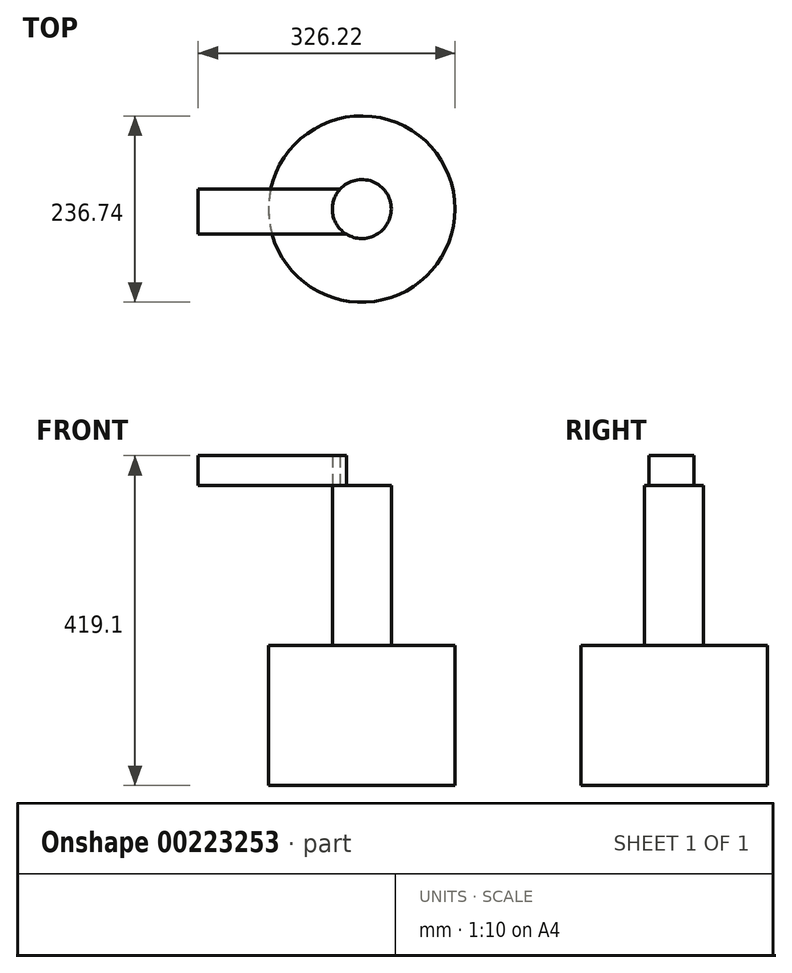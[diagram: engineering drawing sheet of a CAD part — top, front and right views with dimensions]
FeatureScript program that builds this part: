
annotation { "Feature Type Name" : "Feature", "Feature Type Description" : "" }
export const myFeature = defineFeature(function(context is Context, id is Id, definition is map)
    precondition{}
    {
        {
            var Q0;
            Q0=qCreatedBy(makeId("Top.planeOp"),FACE);
            var sketch = newSketch(context, id + "F0", { "sketchPlane" : qUnion([Q0])});
            skCircle(sketch, "E0", {"center": v(0, 0) * mm, "radius": 118.37 * mm});
            skSolve(sketch);
        }
        {
            var Q0;
            Q0=makeQuery(id+"F0.imprint","IMPRINT",FACE,{"disambiguationData":[TD([[makeQuery(id+"F0.imprint","IMPRINT",EDGE,{"derivedFrom":sQuery(id+"F0.wireOp",EDGE,"E0")}),1.0]])]});
            extrude(context, id + "F1", {"entities" : qUnion([Q0]), "depth" : 177.8 * mm});
        }
        {
            var Q0;
            Q0=makeQuery(id+"F1.opExtrude","CAP_FACE",FACE,{"disambiguationData":[OSD([sQuery(id+"F0.wireOp",EDGE,"E0")])],"isStart":false});
            var sketch = newSketch(context, id + "F2", { "sketchPlane" : qUnion([Q0])});
            skCircle(sketch, "E1", {"center": v(0, 0) * mm, "radius": 37.45 * mm});
            skSolve(sketch);
        }
        {
            var Q0;
            Q0=makeQuery(id+"F2.imprint","IMPRINT",FACE,{"disambiguationData":[TD([[makeQuery(id+"F2.imprint","IMPRINT",EDGE,{"derivedFrom":sQuery(id+"F2.wireOp",EDGE,"E1")}),1.0]])]});
            extrude(context, id + "F3", {"entities" : qUnion([Q0]), "operationType" : NewBodyOperationType.ADD, "depth" : 203.2 * mm});
        }
        {
            var Q0;
            Q0=makeQuery(id+"F3.opExtrude","CAP_FACE",FACE,{"disambiguationData":[OSD([sQuery(id+"F2.wireOp",EDGE,"E1")])],"isStart":false});
            var sketch = newSketch(context, id + "F4", { "sketchPlane" : qUnion([Q0])});
            skLineSegment(sketch, "E2.top", {"start": v(0, 25.23) * mm, "end": v(83.63, 25.23) * mm});
            skLineSegment(sketch, "E2.right", {"start": v(83.63, 0) * mm, "end": v(83.63, 25.23) * mm});
            skLineSegment(sketch, "E3.top", {"start": v(0, -32.01) * mm, "end": v(-207.85, -32.01) * mm});
            skLineSegment(sketch, "E3.right", {"start": v(-207.85, 0) * mm, "end": v(-207.85, -32.01) * mm});
            skLineSegment(sketch, "E4.bottom", {"start": v(83.63, 25.23) * mm, "end": v(-207.85, 25.23) * mm});
            skLineSegment(sketch, "E4.top", {"start": v(83.63, -32.01) * mm, "end": v(-207.85, -32.01) * mm});
            skLineSegment(sketch, "E4.left", {"start": v(83.63, 25.23) * mm, "end": v(83.63, -32.01) * mm});
            skLineSegment(sketch, "E4.right", {"start": v(-207.85, 25.23) * mm, "end": v(-207.85, -32.01) * mm});
            skSolve(sketch);
        }
        {
            var Q0;
            {var subQ0=sQuery(id+"F4.wireOp",EDGE,"E4.right");var subQ1=sQuery(id+"F4.wireOp",EDGE,"E4.bottom");var subQ2=makeQuery(id+"F4.imprint","INTERSECT",VERTEX,{"derivedFrom":[subQ1,subQ0]});Q0=makeQuery(id+"F4.imprint","IMPRINT",FACE,{"disambiguationData":[TD([[makeQuery(id+"F4.imprint","IMPRINT",EDGE,{"disambiguationData":[TD([[subQ2,1.0]])],"derivedFrom":subQ1}),1.0]])]});}
            var Q1;
            {var subQ0=sQuery(id+"F4.wireOp",EDGE,"E4.left");var subQ1=sQuery(id+"F4.wireOp",EDGE,"E4.bottom");var subQ2=makeQuery(id+"F4.imprint","INTERSECT",VERTEX,{"derivedFrom":[subQ1,subQ0]});Q1=makeQuery(id+"F4.imprint","IMPRINT",FACE,{"disambiguationData":[TD([[makeQuery(id+"F4.imprint","IMPRINT",EDGE,{"disambiguationData":[TD([[subQ2,-1.0]])],"derivedFrom":subQ1}),1.0]])]});}
            var Q2;
            {var subQ4=sQuery(id+"F4.wireOp",EDGE,"E4.bottom");var subQ8=makeQuery(id+"F4.imprint","IMPRINT",VERTEX,{"derivedFrom":subQ4});Q2=makeQuery(id+"F4.imprint","IMPRINT",FACE,{"disambiguationData":[TD([[makeQuery(id+"F4.imprint","IMPRINT",EDGE,{"disambiguationData":[TD([[subQ8,1.0]])],"derivedFrom":subQ4}),1.0]])]});}
            extrude(context, id + "F5", {"entities" : qUnion([Q0, Q1, Q2]), "operationType" : NewBodyOperationType.ADD, "depth" : 38.1 * mm});
        }
    });
